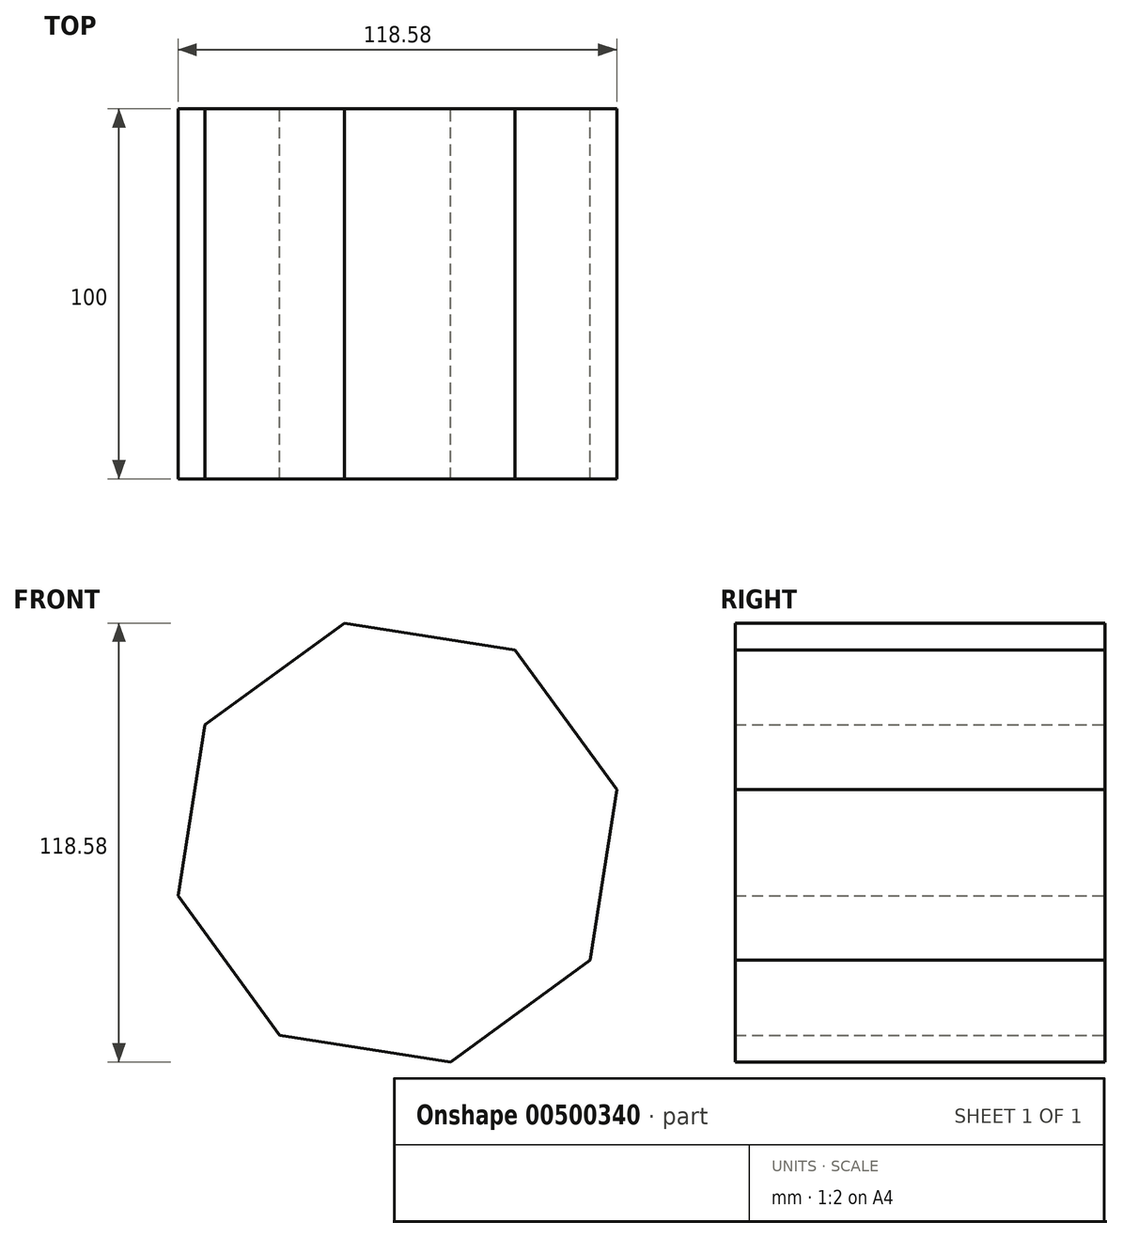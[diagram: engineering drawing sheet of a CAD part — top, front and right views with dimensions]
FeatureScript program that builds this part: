
annotation { "Feature Type Name" : "Feature", "Feature Type Description" : "" }
export const myFeature = defineFeature(function(context is Context, id is Id, definition is map)
    precondition{}
    {
        {
            var Q0;
            Q0=qCreatedBy(makeId("Front.planeOp"),FACE);
            var sketch = newSketch(context, id + "F0", { "sketchPlane" : qUnion([Q0])});
            skCircle(sketch, "E0.cCircle", {"center": v(0, 0) * mm, "radius": 61 * mm, "construction": true});
            skLineSegment(sketch, "E0.0", {"start": v(-31.8, -52.05) * mm, "end": v(-59.3, -14.32) * mm});
            skLineSegment(sketch, "E0.1", {"start": v(-59.3, -14.32) * mm, "end": v(-52.05, 31.8) * mm});
            skLineSegment(sketch, "E0.2", {"start": v(-52.05, 31.8) * mm, "end": v(-14.32, 59.3) * mm});
            skLineSegment(sketch, "E0.3", {"start": v(-14.32, 59.3) * mm, "end": v(31.8, 52.05) * mm});
            skLineSegment(sketch, "E0.4", {"start": v(31.8, 52.05) * mm, "end": v(59.3, 14.32) * mm});
            skLineSegment(sketch, "E0.5", {"start": v(59.3, 14.32) * mm, "end": v(52.05, -31.8) * mm});
            skLineSegment(sketch, "E0.6", {"start": v(52.05, -31.8) * mm, "end": v(14.32, -59.3) * mm});
            skLineSegment(sketch, "E0.7", {"start": v(14.32, -59.3) * mm, "end": v(-31.8, -52.05) * mm});
            skSolve(sketch);
        }
        {
            var Q0;
            Q0=makeQuery(id+"F0.imprint","IMPRINT",FACE,{"disambiguationData":[TD([[makeQuery(id+"F0.imprint","IMPRINT",EDGE,{"derivedFrom":sQuery(id+"F0.wireOp",EDGE,"E0.0")}),-1.0]])]});
            extrude(context, id + "F1", {"entities" : qUnion([Q0]), "depth" : 100 * mm});
        }
    });
